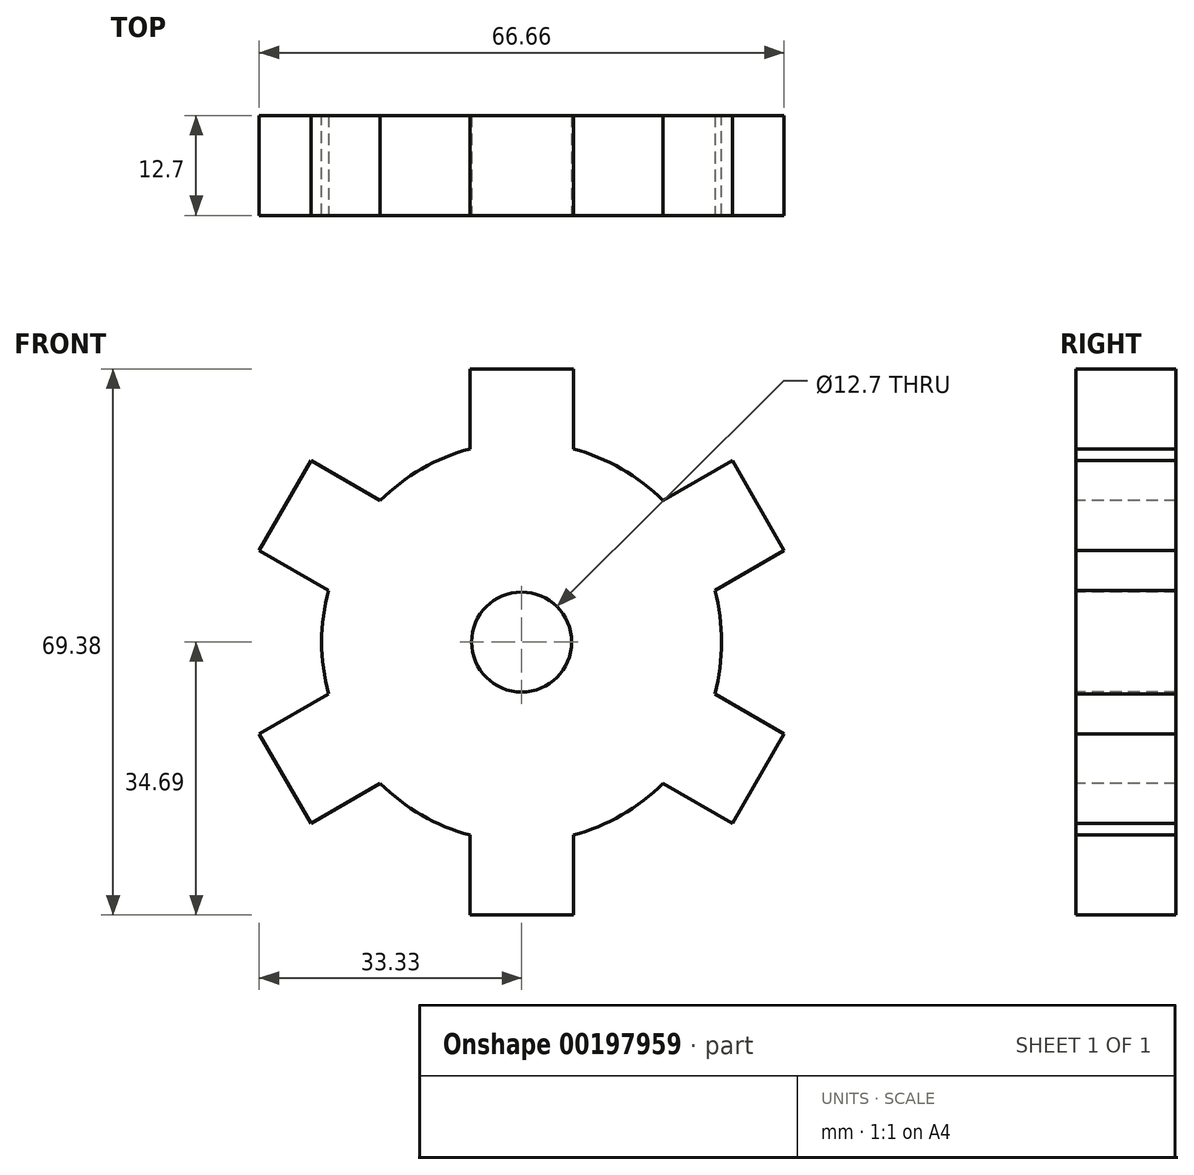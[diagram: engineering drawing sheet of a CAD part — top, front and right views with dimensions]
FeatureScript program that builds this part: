
annotation { "Feature Type Name" : "Feature", "Feature Type Description" : "" }
export const myFeature = defineFeature(function(context is Context, id is Id, definition is map)
    precondition{}
    {
        {
            var Q0;
            Q0=qCreatedBy(makeId("Front.planeOp"),FACE);
            var sketch = newSketch(context, id + "F0", { "sketchPlane" : qUnion([Q0])});
            skCircle(sketch, "E0", {"center": v(0, 0) * mm, "radius": 25.4 * mm});
            skSolve(sketch);
        }
        {
            var Q0;
            Q0 = qSketchRegion(id + "F0", true);
            extrude(context, id + "F1", {"entities" : qUnion([Q0]), "depth" : 12.7 * mm});
        }
        {
            var Q0;
            Q0=makeQuery(id+"F1.opExtrude","CAP_FACE",FACE,{"disambiguationData":[OSD([sQuery(id+"F0.wireOp",EDGE,"E0")])],"isStart":false});
            var sketch = newSketch(context, id + "F2", { "sketchPlane" : qUnion([Q0])});
            skLineSegment(sketch, "E1", {"start": v(0, 0) * mm, "end": v(0, 25.4) * mm});
            skLineSegment(sketch, "E2", {"start": v(0, 25.4) * mm, "end": v(0, 0) * mm});
            skLineSegment(sketch, "E3", {"start": v(0, 0) * mm, "end": v(6.57, 24.53) * mm});
            skLineSegment(sketch, "E4", {"start": v(6.57, 24.53) * mm, "end": v(0, 0) * mm});
            skLineSegment(sketch, "E5", {"start": v(0, 0) * mm, "end": v(-6.57, 24.53) * mm});
            skLineSegment(sketch, "E6", {"start": v(-6.57, 24.53) * mm, "end": v(0, 0) * mm});
            skLineSegment(sketch, "E7", {"start": v(-6.57, 24.53) * mm, "end": v(6.57, 24.53) * mm});
            skLineSegment(sketch, "E8.0", {"start": v(-6.57, 34.7) * mm, "end": v(6.57, 34.7) * mm});
            skLineSegment(sketch, "E9", {"start": v(-6.57, 34.7) * mm, "end": v(-6.57, 24.53) * mm});
            skLineSegment(sketch, "E10", {"start": v(6.57, 34.7) * mm, "end": v(6.57, 24.53) * mm});
            skSolve(sketch);
        }
        {
            var Q0;
            Q0 = qSketchRegion(id + "F2", true);
            extrude(context, id + "F3", {"entities" : qUnion([Q0]), "operationType" : NewBodyOperationType.ADD, "oppositeDirection" : true, "depth" : 12.7 * mm});
        }
        {
            var Q0;
            Q0=qCreatedBy(makeId("Top.planeOp"),FACE);
            var sketch = newSketch(context, id + "F4", { "sketchPlane" : qUnion([Q0])});
            skLineSegment(sketch, "E11", {"start": v(0, 0) * mm, "end": v(0, -67.79) * mm});
            skLineSegment(sketch, "E12", {"start": v(0, -67.79) * mm, "end": v(0, 0) * mm});
            skLineSegment(sketch, "E13", {"start": v(100.45, -22.06) * mm, "end": v(100.45, -14.66) * mm});
            skSolve(sketch);
        }
        {
            var Q0;
            Q0 = qSketchRegion(id + "F2", true);
            extrude(context, id + "F5", {"entities" : qUnion([Q0]), "operationType" : NewBodyOperationType.ADD, "oppositeDirection" : true, "depth" : 12.7 * mm});
        }
        {
            var Q0;
            Q0=makeQuery(id+"F1.opExtrude","SWEPT_BODY",BODY,{"disambiguationData":[OSD([sQuery(id+"F0.wireOp",EDGE,"E0")])]});
            var Q1;
            Q1=sQuery(id+"F4.wireOp",EDGE,"E12");
            circularPattern(context, id + "F6", {"operationType" : NewBodyOperationType.ADD, "entities" : qUnion([Q0]), "axis" : qUnion([Q1]), "angle" : 360 * degree, "instanceCount" : 6, "equalSpace" : true});
        }
        {
            var Q0;
            {var subQ0=makeQuery(id+"F3.boolean.opBoolean","MERGE",FACE,{"derivedFrom":[makeQuery(id+"F1.opExtrude","CAP_FACE",FACE,{"disambiguationData":[OSD([sQuery(id+"F0.wireOp",EDGE,"E0")])],"isStart":false}),makeQuery(id+"F3.opExtrude","CAP_FACE",FACE,{"disambiguationData":[OSD([sQuery(id+"F2.wireOp",EDGE,"E4"),sQuery(id+"F2.wireOp",EDGE,"E6"),sQuery(id+"F2.wireOp",EDGE,"E8.0"),sQuery(id+"F2.wireOp",EDGE,"E9"),sQuery(id+"F2.wireOp",EDGE,"E10")])],"isStart":true})]});Q0=makeQuery(id+"F6.boolean.opBoolean","MERGE",FACE,{"derivedFrom":[subQ0,makeQuery(id+"F6.opPattern","COPY",FACE,{"derivedFrom":subQ0,"instanceName":"1"}),makeQuery(id+"F6.opPattern","COPY",FACE,{"derivedFrom":subQ0,"instanceName":"2"}),makeQuery(id+"F6.opPattern","COPY",FACE,{"derivedFrom":subQ0,"instanceName":"3"}),makeQuery(id+"F6.opPattern","COPY",FACE,{"derivedFrom":subQ0,"instanceName":"4"}),makeQuery(id+"F6.opPattern","COPY",FACE,{"derivedFrom":subQ0,"instanceName":"5"})]});}
            var sketch = newSketch(context, id + "F7", { "sketchPlane" : qUnion([Q0])});
            skCircle(sketch, "E14", {"center": v(0, 0) * mm, "radius": 6.35 * mm});
            skSolve(sketch);
        }
        {
            var Q0;
            Q0 = qSketchRegion(id + "F7", true);
            extrude(context, id + "F8", {"entities" : qUnion([Q0]), "operationType" : NewBodyOperationType.REMOVE, "oppositeDirection" : true, "depth" : 25.4 * mm});
        }
    });
